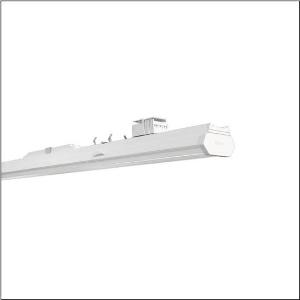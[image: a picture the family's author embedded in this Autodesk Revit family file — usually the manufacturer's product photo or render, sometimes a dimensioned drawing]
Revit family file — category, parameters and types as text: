
# Revit family: licross_r__21_protected_mo_52td1bdn4axg_daa2
name_source: partatom
category: Lighting Fixtures
units: mm (PartAtom-declared; Revit-internal decimal feet)

## family parameters
Cut with Voids When Loaded = No
Host = Face
Light Source = No
Part Type = Normal
Room Calculation Point = No
Round Connector Dimension = Use Diameter
Shared = No

## types (1)
- --- (1 x LED, 10050 lm, 62 W, 4000K)
    Apparent Load = 62 VA
    CIE Flux Codes = 54 82 95 97 100
    Color Rendering = 80
    Color Temperature = 4000K
    Default Elevation = 1800 mm
    Description = Licross® 21 Protected MO, luminaire insert, of sheet steel, galvanised, coil coated, white, length: 1.500mm, width: 90mm, height: 103mm, LED rated luminous flux: 10.060lm, light colour: 840, control gear: DALI 2, with plug, 5-pole, with phase selection, mains connection: 220..240V, AC, 50/60Hz, rated input power: 62W, halogen-free wiring, primary optical cover: cover, of PMMA, light emission: direct distribution, primary light characteristic: symmetric, protection rating (complete): IP54, insulation class (complete): insulation class I (protective earthing), certification: CE, ENEC, VDE, UKCA, protection symbol: D if used in an environment with non-conductive dust loads with corresponding accessories, impact resistance: IK06, permissible ambient temperature for indoor applications: -25..+35°C, corresponds to IFS (International Featured Standards) requirements for safety and quality in the food industry, reducing of maximum allowable ambient temperature of 5°C with ceiling mounting, LABS conformity tested according to VDMA 24364:2018-05, packaging unit: 1 piece
    Height = 92 mm
    Lamp = 1 x LED
    Lamp Light Flux = 10050 lm
    Lamp Power = 62 W
    Lamp count = 1
    Length = 1500 mm
    Luminous efficacy = 162 lm/W
    Manufacturer = Siteco
    ModVariant = No
    Model = 52TD1BDN4AXG
    Mounting Place = Ceiling
    Mounting Type = Pendant
    Number of Poles = 1
    OnlyDefault = Yes
    Power Factor = 1
    Product Name = Licross® 21 Protected MO
    Product group = luminaire insert
    ProductGroupID = 901
    Protection Class = Protection class I
    Protection Degree = IP 54
    RLX_Detail_Level = 1
    RLX_Emergency_Light_Flux = 0 lm
    RLX_Emergency_Type = 0
    RLX_Emergency_Type_DB = No
    RlxData = <blob elided: 24265 chars, md5=4450edb4>
    Socket = socket
    Standby Power = 0 W
    System Light Flux = 10050 lm
    System Power = 62 W
    Type Comments = factory setting: luminous flux: 100 % | dim-lin: 254 | 418 mA
    Type Image = l_1256148.jpg
    URL = http://relux.com
    VarID = @adj_078747
    Voltage = 0 V
    Weight = 0.00 kg
    Width = 88 mm

## geometry (parser evidence)
native form markers: Blend x4, Sweep x10
no freeform markers — native parametric forms only
